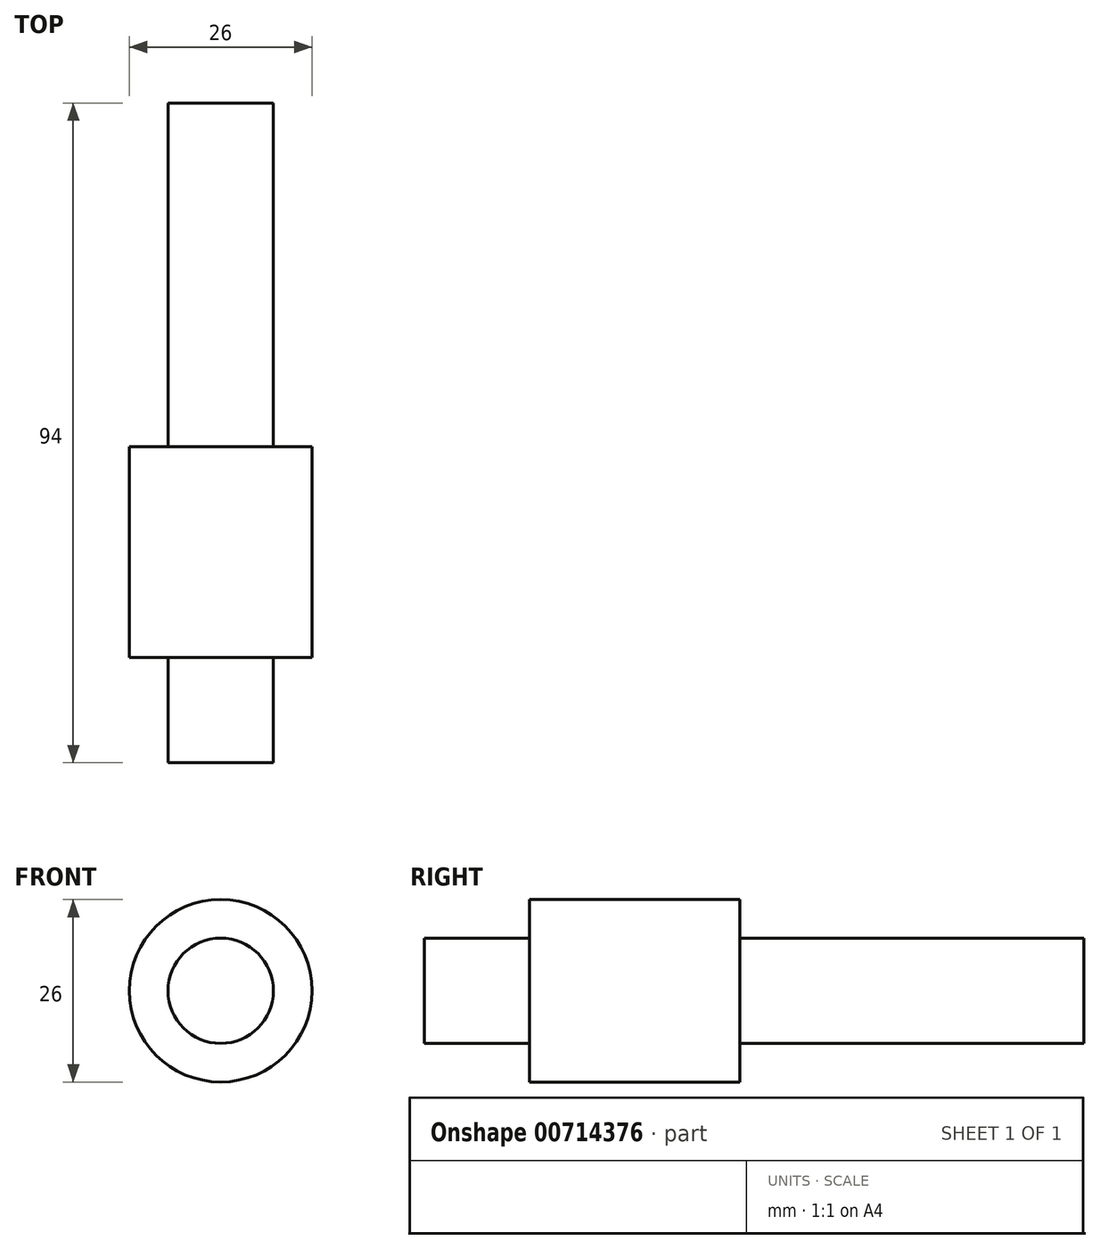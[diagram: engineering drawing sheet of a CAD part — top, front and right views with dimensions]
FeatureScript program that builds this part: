
annotation { "Feature Type Name" : "Feature", "Feature Type Description" : "" }
export const myFeature = defineFeature(function(context is Context, id is Id, definition is map)
    precondition{}
    {
        {
            var Q0;
            Q0=qCreatedBy(makeId("Front.planeOp"),FACE);
            var sketch = newSketch(context, id + "F0", { "sketchPlane" : qUnion([Q0])});
            skCircle(sketch, "E0", {"center": v(0, 0) * mm, "radius": 13 * mm});
            skSolve(sketch);
        }
        {
            var Q0;
            Q0=makeQuery(id+"F0.imprint","IMPRINT",FACE,{"disambiguationData":[TD([[makeQuery(id+"F0.imprint","IMPRINT",EDGE,{"derivedFrom":sQuery(id+"F0.wireOp",EDGE,"E0")}),1.0]])]});
            var Q1;
            Q1=sQuery(id+"F0.wireOp",EDGE,"E0");
            extrude(context, id + "F1", {"entities" : qUnion([Q0]), "surfaceEntities" : qUnion([Q1]), "depth" : 94 * mm, "offsetDistance" : 25 * mm});
        }
        {
            var Q0;
            Q0=makeQuery(id+"F1.opExtrude","CAP_FACE",FACE,{"disambiguationData":[OSD([sQuery(id+"F0.wireOp",EDGE,"E0")])],"isStart":false});
            var sketch = newSketch(context, id + "F2", { "sketchPlane" : qUnion([Q0])});
            skCircle(sketch, "E1", {"center": v(0, 0) * mm, "radius": 7.5 * mm});
            skSolve(sketch);
        }
        {
            var Q0;
            Q0=makeQuery(id+"F2.imprint","IMPRINT",FACE,{"disambiguationData":[TD([[makeQuery(id+"F2.imprint","IMPRINT",EDGE,{"derivedFrom":sQuery(id+"F2.wireOp",EDGE,"E1")}),-1.0]])]});
            extrude(context, id + "F3", {"entities" : qUnion([Q0]), "operationType" : NewBodyOperationType.REMOVE, "oppositeDirection" : true, "depth" : 15 * mm, "offsetDistance" : 25 * mm});
        }
        {
            var Q0;
            Q0=makeQuery(id+"F1.opExtrude","CAP_FACE",FACE,{"disambiguationData":[OSD([sQuery(id+"F0.wireOp",EDGE,"E0")])],"isStart":true});
            var sketch = newSketch(context, id + "F4", { "sketchPlane" : qUnion([Q0])});
            skCircle(sketch, "E2", {"center": v(0, 0) * mm, "radius": 7.5 * mm});
            skSolve(sketch);
        }
        {
            var Q0;
            Q0=makeQuery(id+"F4.imprint","IMPRINT",FACE,{"disambiguationData":[TD([[makeQuery(id+"F4.imprint","IMPRINT",EDGE,{"derivedFrom":sQuery(id+"F4.wireOp",EDGE,"E2")}),-1.0]])]});
            extrude(context, id + "F5", {"entities" : qUnion([Q0]), "operationType" : NewBodyOperationType.REMOVE, "oppositeDirection" : true, "depth" : 49 * mm, "offsetDistance" : 25 * mm});
        }
    });
